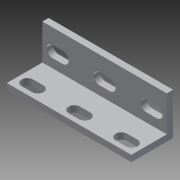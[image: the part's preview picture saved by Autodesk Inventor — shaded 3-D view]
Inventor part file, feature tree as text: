
AUTODESK INVENTOR PART (.ipt)
format: ipt  version: 2014 SP1 (Build 180222100, 222)  size: 150,016 bytes
history: native  units: in
note: dims shown in document units (in); Inventor stores cm internally (conversion verified against a paired STEP export)
features: extrude x3, sketch x3
ambient origin geometry x8: Origin, YZ Plane, XZ Plane, XY Plane, X Axis, Y Axis, Z Axis, Center Point
bodies: Solid1 (feature_tree)
feature tree (6):
  extrude  "Extrusion1"  Depth=2.3465in
  extrude  "Extrusion2"  Depth=0.1181in
  extrude  "Extrusion3"  Depth=0.2165in
  sketch  "Sketch1"  dims[d0=0.7874in d1=2.3465in]
  sketch  "Sketch2"  dims[d5=0.1181in d6=0.0in d7=0.1181in]
  sketch  "Sketch3"  dims[d8=0.6693in d9=0.0in d12=0.1969in d13=0.6693in d14=0.0in d17=0.1969in d18=0.2165in d19=0.2165in d20=0.1969in d21=0.2165in d22=0.1969in d23=0.8858in d24=0.8858in d25=0.1969in d26=0.2165in d27=0.1969in d28=0.2165in d29=0.1969in d30=0.2165in d31=0.8858in d32=0.8858in]
